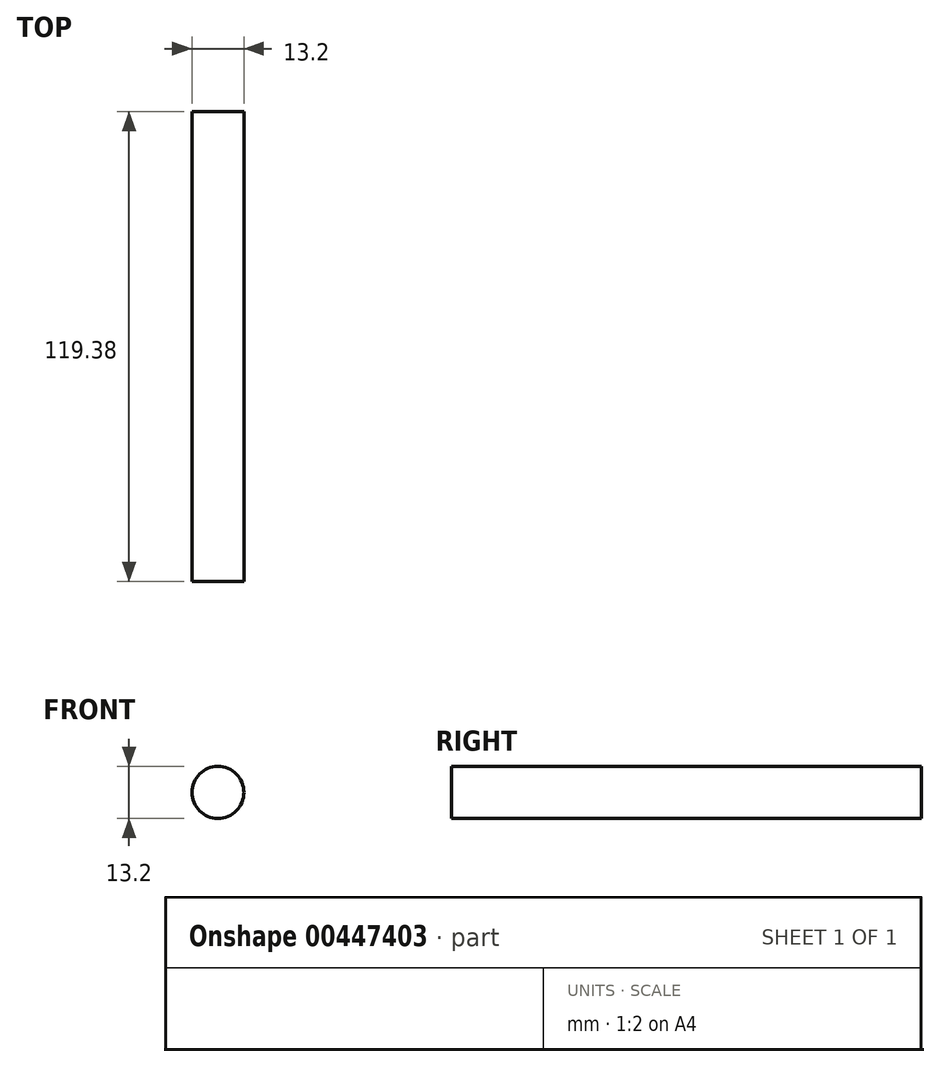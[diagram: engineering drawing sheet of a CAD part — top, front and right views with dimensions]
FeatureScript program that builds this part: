
annotation { "Feature Type Name" : "Feature", "Feature Type Description" : "" }
export const myFeature = defineFeature(function(context is Context, id is Id, definition is map)
    precondition{}
    {
        {
            var Q0;
            Q0=qCreatedBy(makeId("Front.planeOp"),FACE);
            var sketch = newSketch(context, id + "F0", { "sketchPlane" : qUnion([Q0])});
            skCircle(sketch, "E0", {"center": v(0, 0) * mm, "radius": 6.6 * mm});
            skSolve(sketch);
        }
        {
            var Q0;
            Q0 = qSketchRegion(id + "F0", true);
            extrude(context, id + "F1", {"entities" : qUnion([Q0]), "depth" : 119.38 * mm});
        }
    });
